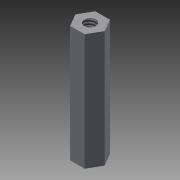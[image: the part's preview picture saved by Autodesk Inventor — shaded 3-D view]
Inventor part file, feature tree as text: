
AUTODESK INVENTOR PART (.ipt)
format: ipt  version: 2015 (Build 190159000, 159)  size: 81,920 bytes
history: native  units: in
note: dims shown in document units (in); Inventor stores cm internally (conversion verified against a paired STEP export)
features: sketch x2, extrude x1, hole x1, projected_geometry x1
ambient origin geometry x8: Origin, YZ Plane, XZ Plane, XY Plane, X Axis, Y Axis, Z Axis, Center Point
bodies: Solid1 (feature_tree)
feature tree (5):
  extrude  "Extrusion1"  Depth=0.1083in
  hole  "Hole1"  [1 undecoded]
  sketch  "Sketch2"  dims[d0=0.25in d1=0.1083in]
  sketch  "Sketch3"  dims[d2=1.0in d3=0.0in d4=0.098in d5=0.25in d6=0.375in d7=0.25in d8=0.5635in d9=0.375in d10=0.8108in]
  projected_geometry  "Projected Loop1"
note: 1 required parameter value undecoded (feature->parameter linkage not recoverable at this tier; creation-order binding heuristic only, values carry confidence <= 0.55)
